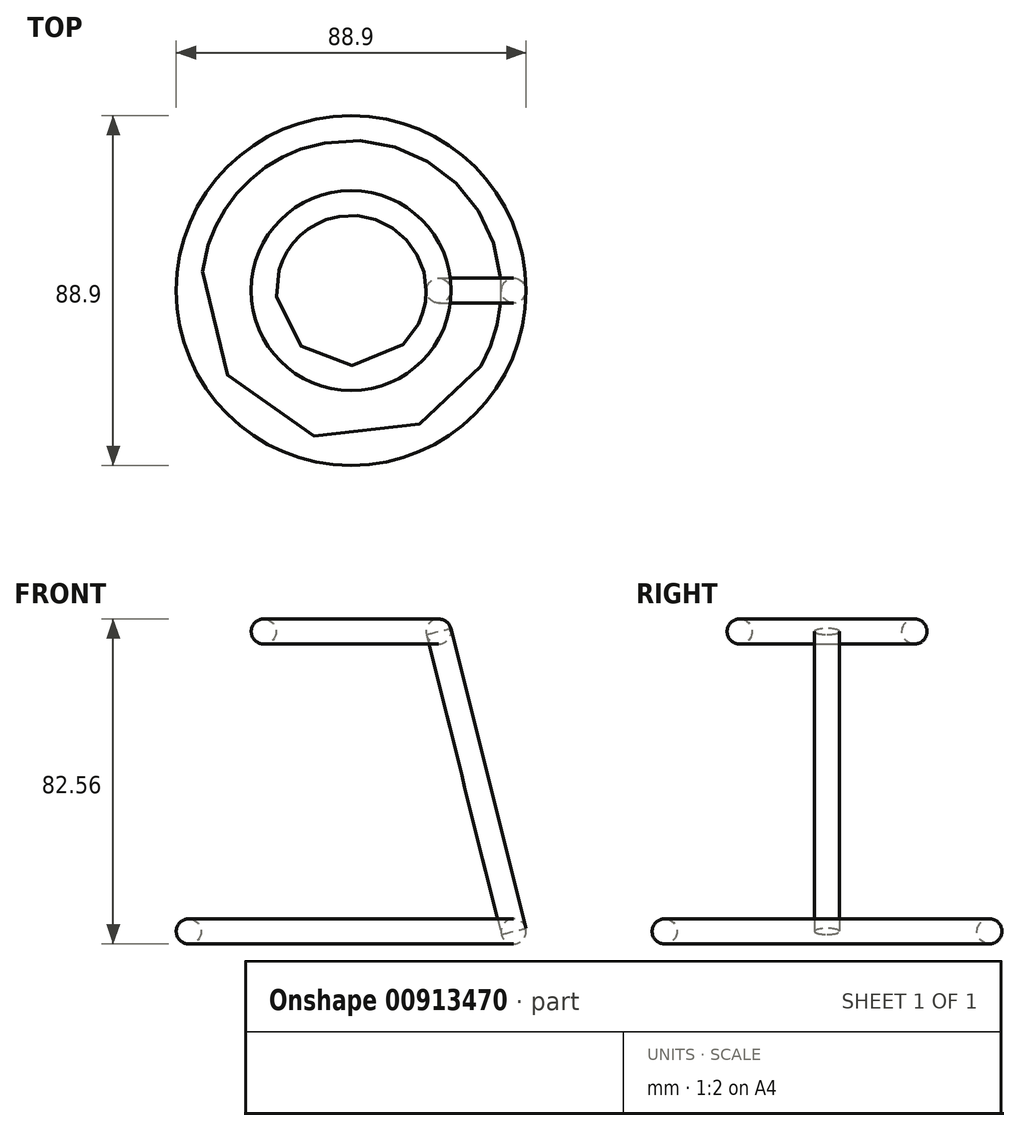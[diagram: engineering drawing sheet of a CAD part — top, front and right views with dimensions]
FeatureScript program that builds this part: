
annotation { "Feature Type Name" : "Feature", "Feature Type Description" : "" }
export const myFeature = defineFeature(function(context is Context, id is Id, definition is map)
    precondition{}
    {
        {
            var Q0;
            Q0=qCreatedBy(makeId("Front.planeOp"),FACE);
            var sketch = newSketch(context, id + "F0", { "sketchPlane" : qUnion([Q0])});
            skCircle(sketch, "E0", {"center": v(22.23, 76.2) * mm, "radius": 3.18 * mm});
            skLineSegment(sketch, "E1", {"start": v(0, 49.86) * mm, "end": v(0, 14.24) * mm});
            skCircle(sketch, "E2", {"center": v(41.27, 0) * mm, "radius": 3.18 * mm});
            skSolve(sketch);
        }
        {
            var Q0;
            Q0 = qSketchRegion(id + "F0", true);
            var Q1;
            Q1=sQuery(id+"F0.wireOp",EDGE,"E1");
            revolve(context, id + "F1", {"surfaceOperationType" : NewSurfaceOperationType.NEW, "entities" : qUnion([Q0]), "axis" : qUnion([Q1]), "revolveType" : RevolveType.FULL});
        }
        {
            var Q0;
            Q0=qCreatedBy(makeId("Front.planeOp"),FACE);
            var sketch = newSketch(context, id + "F2", { "sketchPlane" : qUnion([Q0])});
            skLineSegment(sketch, "E3", {"start": v(41.28, 0) * mm, "end": v(22.22, 76.2) * mm});
            skLineSegment(sketch, "E4", {"start": v(22.22, 76.2) * mm, "end": v(25.3, 76.97) * mm});
            skLineSegment(sketch, "E5", {"start": v(25.3, 76.97) * mm, "end": v(44.36, 0.77) * mm});
            skLineSegment(sketch, "E6", {"start": v(44.36, 0.77) * mm, "end": v(41.27, 0) * mm});
            skSolve(sketch);
        }
        {
            var Q0;
            Q0 = qSketchRegion(id + "F2", true);
            var Q1;
            Q1=sQuery(id+"F2.wireOp",EDGE,"E3");
            revolve(context, id + "F3", {"surfaceOperationType" : NewSurfaceOperationType.NEW, "entities" : qUnion([Q0]), "axis" : qUnion([Q1]), "revolveType" : RevolveType.FULL});
        }
    });
